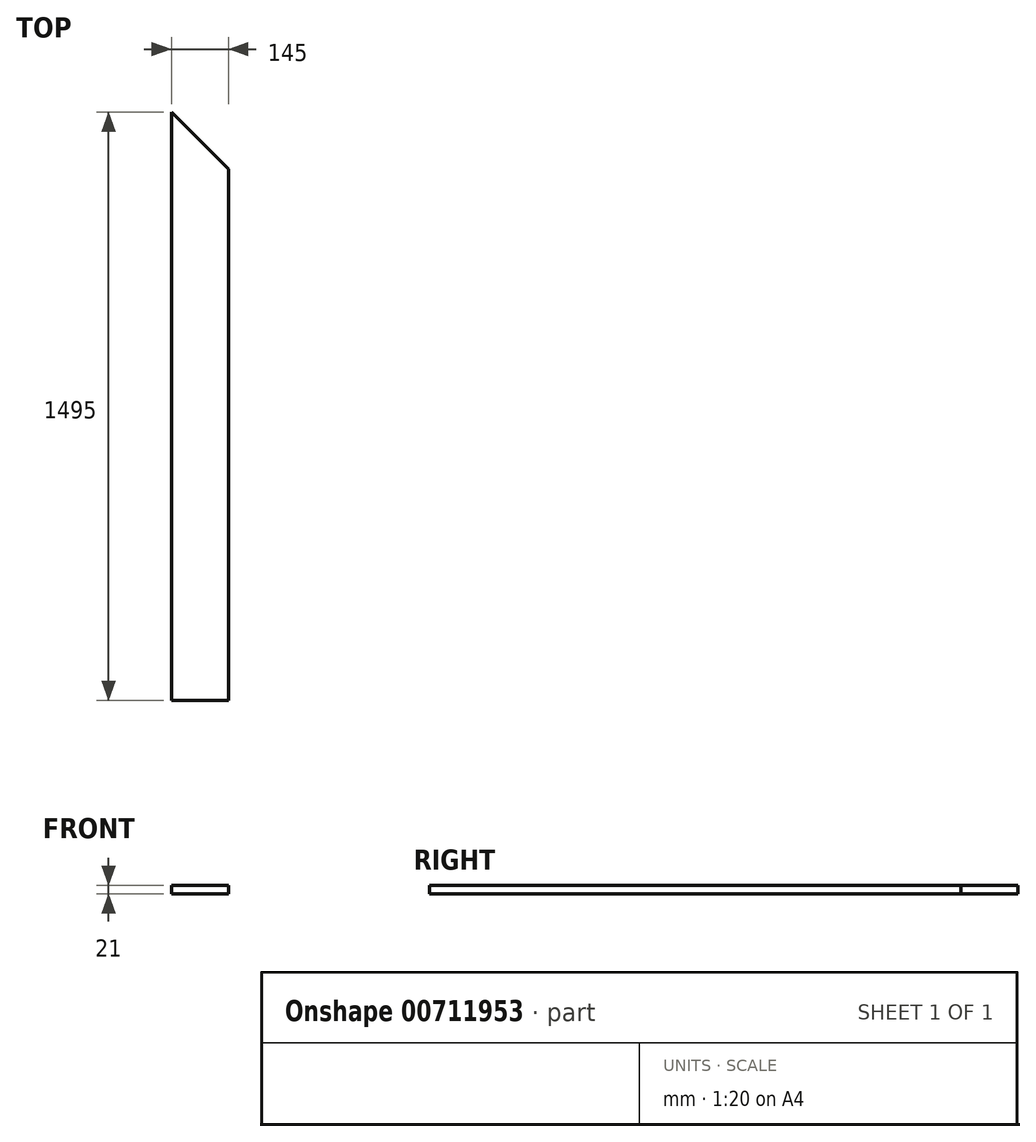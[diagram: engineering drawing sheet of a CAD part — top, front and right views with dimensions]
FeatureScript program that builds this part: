
annotation { "Feature Type Name" : "Feature", "Feature Type Description" : "" }
export const myFeature = defineFeature(function(context is Context, id is Id, definition is map)
    precondition{}
    {
        {
            var Q0;
            Q0=qCreatedBy(makeId("Top.planeOp"),FACE);
            var sketch = newSketch(context, id + "F0", { "sketchPlane" : qUnion([Q0])});
            skLineSegment(sketch, "E0", {"start": v(-72.5, -711.25) * mm, "end": v(-72.5, 783.75) * mm});
            skLineSegment(sketch, "E1", {"start": v(-72.5, 783.75) * mm, "end": v(72.5, 638.75) * mm});
            skLineSegment(sketch, "E2", {"start": v(72.5, 638.75) * mm, "end": v(72.5, -711.25) * mm});
            skLineSegment(sketch, "E3", {"start": v(72.5, -711.25) * mm, "end": v(-72.5, -711.25) * mm});
            skSolve(sketch);
        }
        {
            var Q0;
            Q0 = qSketchRegion(id + "F0", true);
            extrude(context, id + "F1", {"entities" : qUnion([Q0]), "depth" : 21 * mm, "offsetDistance" : 25 * mm});
        }
    });
